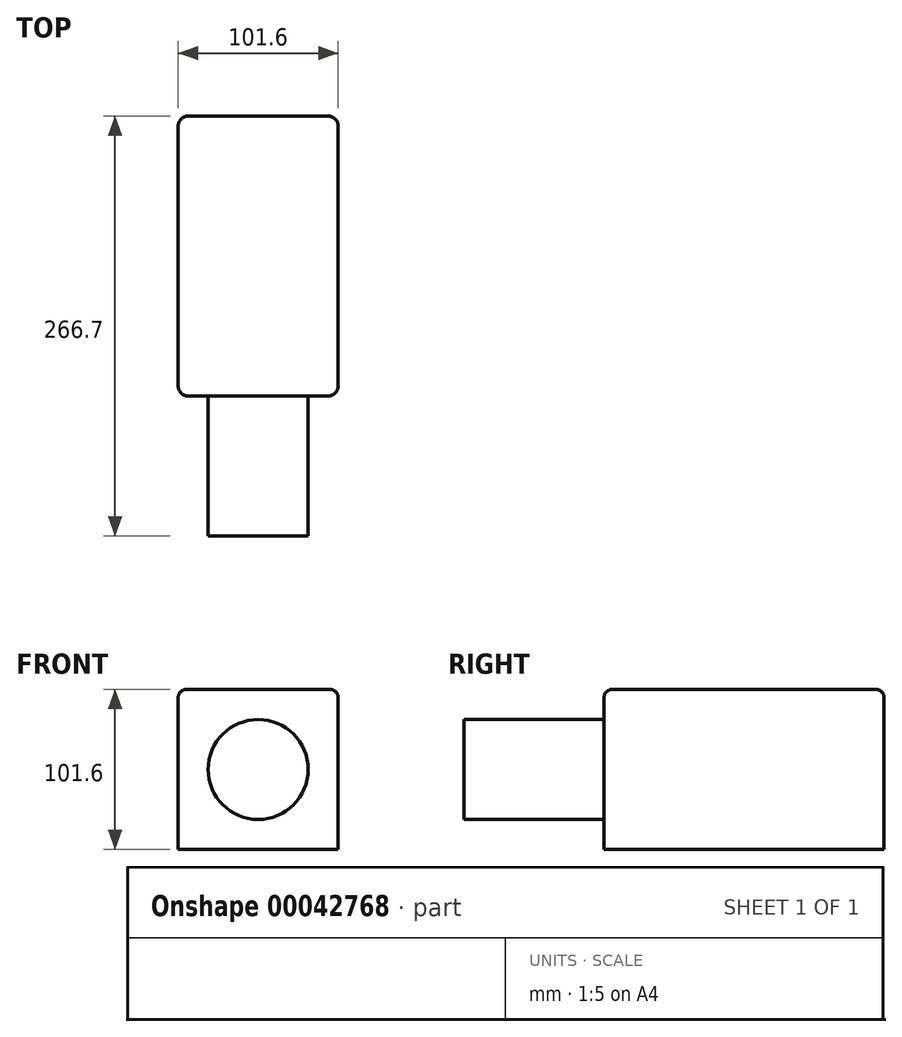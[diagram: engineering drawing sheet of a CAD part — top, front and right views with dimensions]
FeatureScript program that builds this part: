
annotation { "Feature Type Name" : "Feature", "Feature Type Description" : "" }
export const myFeature = defineFeature(function(context is Context, id is Id, definition is map)
    precondition{}
    {
        {
            var Q0;
            Q0=qCreatedBy(makeId("Front.planeOp"),FACE);
            var sketch = newSketch(context, id + "F0", { "sketchPlane" : qUnion([Q0])});
            skLineSegment(sketch, "E0.bottom", {"start": v(-94.4, 63.16) * mm, "end": v(7.2, 63.16) * mm});
            skLineSegment(sketch, "E0.top", {"start": v(-94.4, -38.44) * mm, "end": v(7.2, -38.44) * mm});
            skLineSegment(sketch, "E0.left", {"start": v(-94.4, 63.16) * mm, "end": v(-94.4, -38.44) * mm});
            skLineSegment(sketch, "E0.right", {"start": v(7.2, 63.16) * mm, "end": v(7.2, -38.44) * mm});
            skSolve(sketch);
        }
        {
            var Q0;
            Q0=makeQuery(id+"F0.imprint","IMPRINT",FACE,{"disambiguationData":[TD([[makeQuery(id+"F0.imprint","IMPRINT",EDGE,{"derivedFrom":sQuery(id+"F0.wireOp",EDGE,"E0.bottom")}),-1.0]])]});
            extrude(context, id + "F1", {"entities" : qUnion([Q0]), "oppositeDirection" : true, "depth" : 177.8 * mm});
        }
        {
            var Q0;
            Q0=makeQuery(id+"F1.opExtrude","CAP_FACE",FACE,{"disambiguationData":[OSD([sQuery(id+"F0.wireOp",EDGE,"E0.bottom"),sQuery(id+"F0.wireOp",EDGE,"E0.top"),sQuery(id+"F0.wireOp",EDGE,"E0.left"),sQuery(id+"F0.wireOp",EDGE,"E0.right")])],"isStart":true});
            var sketch = newSketch(context, id + "F2", { "sketchPlane" : qUnion([Q0])});
            skCircle(sketch, "E1", {"center": v(-43.6, 12.36) * mm, "radius": 31.75 * mm});
            skPoint(sketch, "E1.centerSnap0", {"position": v(7.2, 12.36) * mm});
            skPoint(sketch, "E1.centerSnap1", {"position": v(-43.6, 63.16) * mm});
            skSolve(sketch);
        }
        {
            var Q0;
            Q0=makeQuery(id+"F2.imprint","IMPRINT",FACE,{"disambiguationData":[TD([[makeQuery(id+"F2.imprint","IMPRINT",EDGE,{"derivedFrom":sQuery(id+"F2.wireOp",EDGE,"E1")}),1.0]])]});
            extrude(context, id + "F3", {"entities" : qUnion([Q0]), "operationType" : NewBodyOperationType.ADD, "depth" : 88.9 * mm});
        }
        {
            var Q0;
            Q0=makeQuery(id+"F1.opExtrude","CAP_EDGE",EDGE,{"disambiguationData":[OSD([sQuery(id+"F0.wireOp",EDGE,"E0.right")])],"isStart":true});
            var Q1;
            Q1=makeQuery(id+"F1.opExtrude","CAP_EDGE",EDGE,{"disambiguationData":[OSD([sQuery(id+"F0.wireOp",EDGE,"E0.left")])],"isStart":true});
            var Q2;
            Q2=makeQuery(id+"F1.opExtrude","CAP_EDGE",EDGE,{"disambiguationData":[OSD([sQuery(id+"F0.wireOp",EDGE,"E0.right")])],"isStart":false});
            var Q3;
            Q3=makeQuery(id+"F1.opExtrude","CAP_EDGE",EDGE,{"disambiguationData":[OSD([sQuery(id+"F0.wireOp",EDGE,"E0.left")])],"isStart":false});
            fillet(context, id + "F4", {"entities" : qUnion([Q0, Q1, Q2, Q3]), "radius" : 6.35 * mm, "tangentPropagation" : true, "allowEdgeOverflow" : false});
        }
        {
            var Q0;
            Q0=makeQuery(id+"F1.opExtrude","SWEPT_EDGE",EDGE,{"disambiguationData":[OSD([sQuery(id+"F0.wireOp",EDGE,"E0.bottom"),sQuery(id+"F0.wireOp",EDGE,"E0.right")])]});
            fillet(context, id + "F5", {"entities" : qUnion([Q0]), "radius" : 5.08 * mm, "tangentPropagation" : true, "allowEdgeOverflow" : false});
        }
    });
